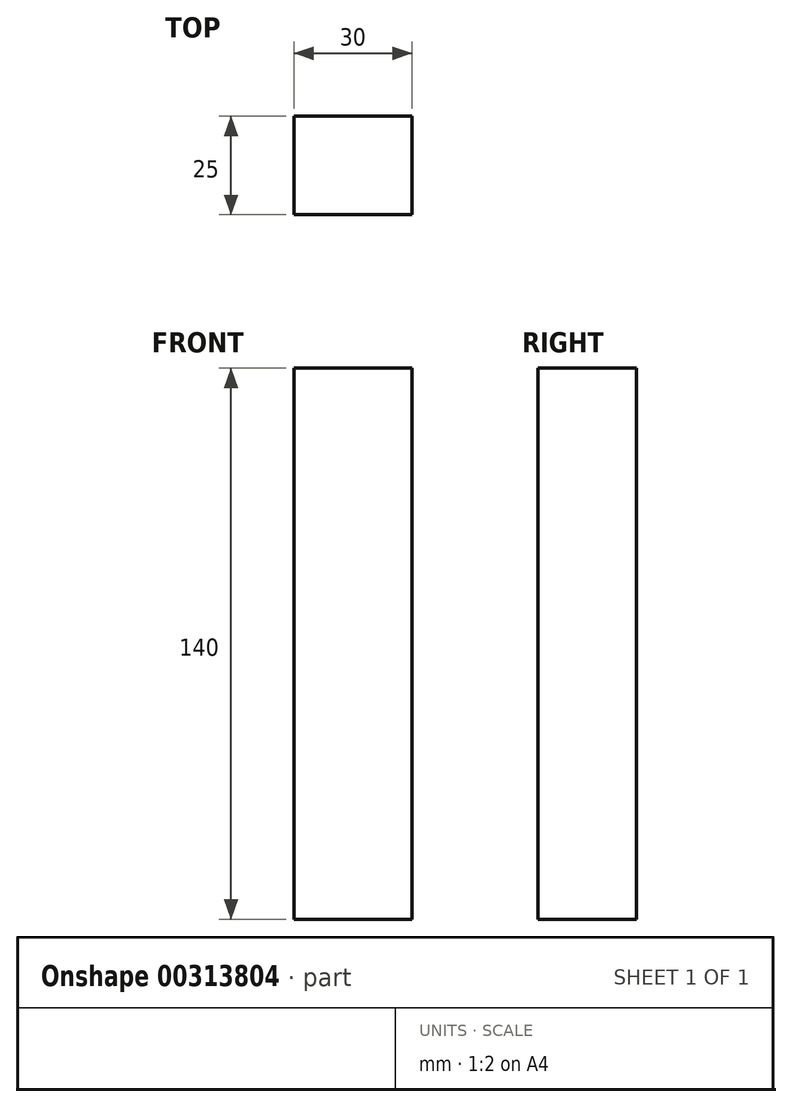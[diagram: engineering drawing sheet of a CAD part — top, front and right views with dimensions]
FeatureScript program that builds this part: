
annotation { "Feature Type Name" : "Feature", "Feature Type Description" : "" }
export const myFeature = defineFeature(function(context is Context, id is Id, definition is map)
    precondition{}
    {
        {
            var Q0;
            Q0=qCreatedBy(makeId("Front.planeOp"),FACE);
            var sketch = newSketch(context, id + "F0", { "sketchPlane" : qUnion([Q0])});
            skLineSegment(sketch, "E0.bottom", {"start": v(-15, 70) * mm, "end": v(15, 70) * mm});
            skLineSegment(sketch, "E0.top", {"start": v(-15, -70) * mm, "end": v(15, -70) * mm});
            skLineSegment(sketch, "E0.left", {"start": v(-15, 70) * mm, "end": v(-15, -70) * mm});
            skLineSegment(sketch, "E0.right", {"start": v(15, 70) * mm, "end": v(15, -70) * mm});
            skPoint(sketch, "E0.middle", {"position": v(0, 0) * mm});
            skSolve(sketch);
        }
        {
            var Q0;
            Q0=makeQuery(id+"F0.imprint","IMPRINT",FACE,{"disambiguationData":[TD([[makeQuery(id+"F0.imprint","IMPRINT",EDGE,{"derivedFrom":sQuery(id+"F0.wireOp",EDGE,"E0.bottom")}),-1.0]])]});
            extrude(context, id + "F1", {"entities" : qUnion([Q0]), "endBound" : BoundingType.SYMMETRIC, "depth" : 25 * mm});
        }
    });
